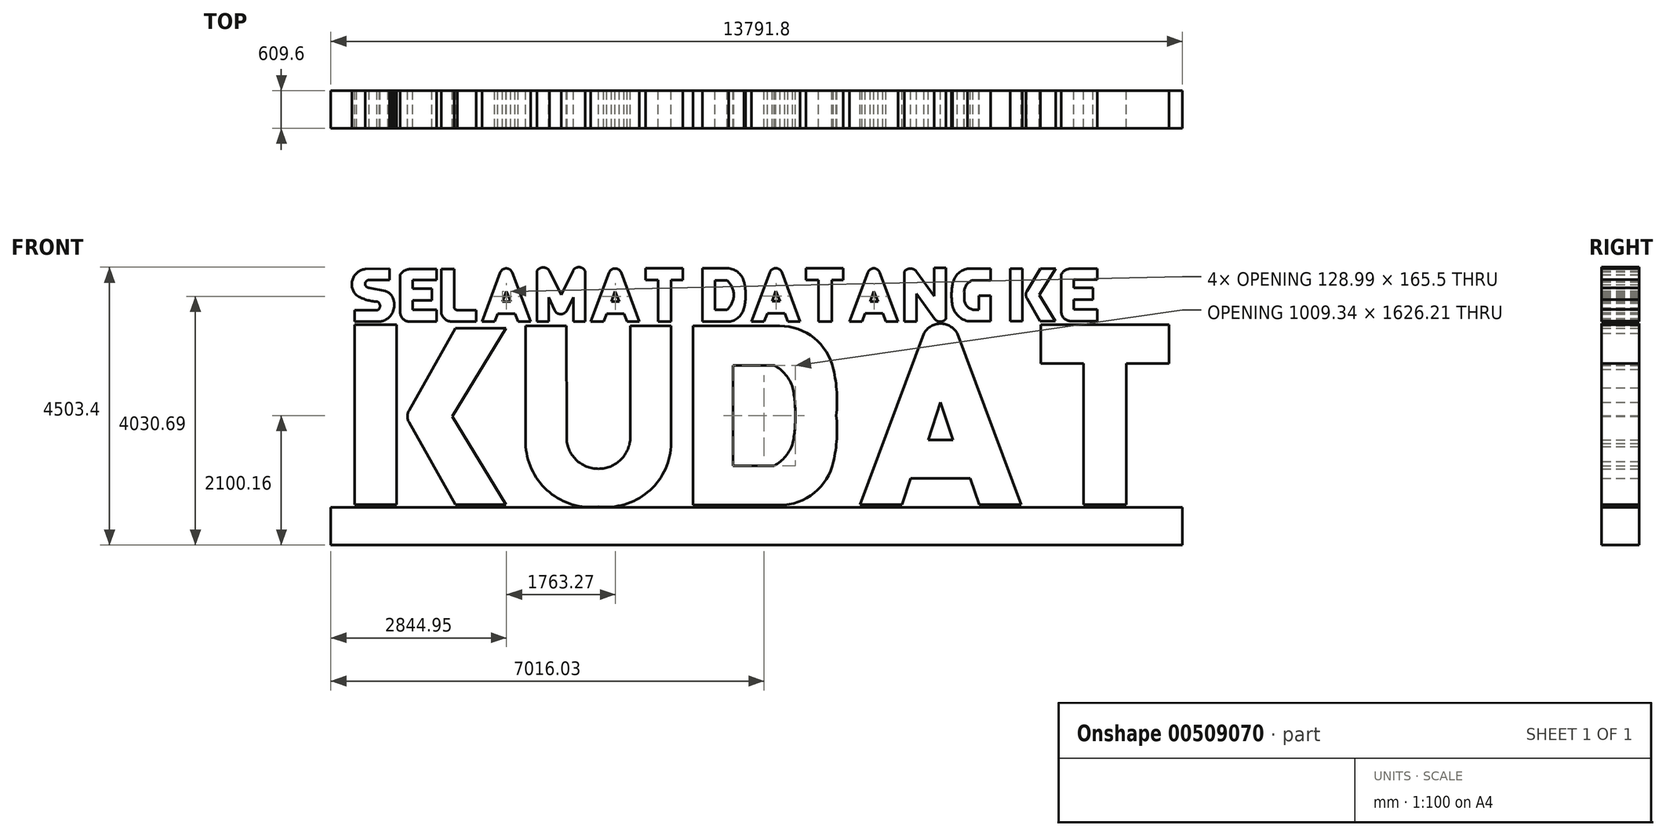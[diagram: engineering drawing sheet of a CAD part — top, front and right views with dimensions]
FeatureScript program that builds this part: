
annotation { "Feature Type Name" : "Feature", "Feature Type Description" : "" }
export const myFeature = defineFeature(function(context is Context, id is Id, definition is map)
    precondition{}
    {
        {
            var Q0;
            Q0=qCreatedBy(makeId("Front.planeOp"),FACE);
            var sketch = newSketch(context, id + "F0", { "sketchPlane" : qUnion([Q0])});
            skLineSegment(sketch, "E0", {"start": v(879.75, 1714.23) * mm, "end": v(879.75, -240.62) * mm});
            skLineSegment(sketch, "E1", {"start": v(-1444.26, -240.62) * mm, "end": v(879.75, -240.62) * mm, "construction": true});
            skLineSegment(sketch, "E2", {"start": v(1236.83, -1188.64) * mm, "end": v(1236.83, 1714.23) * mm});
            skLineSegment(sketch, "E3", {"start": v(1236.83, 1714.23) * mm, "end": v(2637.34, 1714.23) * mm});
            skArc(sketch, "E4", {"start": v(3508.06, 1010.34) * mm, "mid": v(3197.16, 1516.25) * mm, "end": v(2637.34, 1714.23) * mm});
            skLineSegment(sketch, "E5", {"start": v(1236.83, 262.8) * mm, "end": v(3663.8, 262.8) * mm, "construction": true});
            skPoint(sketch, "E5.endSnap0", {"position": v(1236.83, 262.8) * mm});
            skArc(sketch, "E6", {"start": v(3554.76, 262.8) * mm, "mid": v(3561.92, 638.47) * mm, "end": v(3508.06, 1010.34) * mm});
            skArc(sketch, "E7.MirrorCS", {"start": v(3554.76, 262.8) * mm, "mid": v(3561.92, -112.89) * mm, "end": v(3508.06, -484.75) * mm});
            skArc(sketch, "E8.MirrorCS", {"start": v(3508.06, -484.75) * mm, "mid": v(3197.16, -990.66) * mm, "end": v(2637.34, -1188.64) * mm});
            skLineSegment(sketch, "E9.MirrorCS", {"start": v(1236.83, -1188.64) * mm, "end": v(2637.34, -1188.64) * mm});
            skArc(sketch, "E10", {"start": v(2849.13, -189.28) * mm, "mid": v(2883.14, 43.13) * mm, "end": v(2889.18, 277.93) * mm});
            skArc(sketch, "E11", {"start": v(2548.8, -550.31) * mm, "mid": v(2732.4, -397.6) * mm, "end": v(2849.13, -189.28) * mm});
            skLineSegment(sketch, "E12", {"start": v(2548.8, -550.31) * mm, "end": v(1880.98, -550.31) * mm});
            skLineSegment(sketch, "E13", {"start": v(879.75, 1714.23) * mm, "end": v(218.23, 1714.23) * mm});
            skLineSegment(sketch, "E14", {"start": v(218.23, 1714.23) * mm, "end": v(218.23, -87.55) * mm});
            skLineSegment(sketch, "E15", {"start": v(7558.08, 1103.12) * mm, "end": v(7558.08, -1179.44) * mm});
            skLineSegment(sketch, "E16", {"start": v(7558.08, -1179.44) * mm, "end": v(8251.82, -1179.44) * mm});
            skLineSegment(sketch, "E17", {"start": v(7558.08, 1103.12) * mm, "end": v(6867.65, 1103.12) * mm});
            skLineSegment(sketch, "E18", {"start": v(6867.65, 1103.12) * mm, "end": v(6867.65, 1734.9) * mm});
            skLineSegment(sketch, "E19", {"start": v(7904.95, -1179.44) * mm, "end": v(7904.95, 2382.64) * mm, "construction": true});
            skLineSegment(sketch, "E20.MirrorCS", {"start": v(8251.82, 1103.12) * mm, "end": v(8251.82, -1179.44) * mm});
            skLineSegment(sketch, "E21.MirrorCS", {"start": v(8251.82, 1103.12) * mm, "end": v(8942.25, 1103.12) * mm});
            skLineSegment(sketch, "E22.MirrorCS", {"start": v(8942.25, 1103.12) * mm, "end": v(8942.25, 1734.9) * mm});
            skLineSegment(sketch, "E23", {"start": v(6867.65, 1734.9) * mm, "end": v(8942.25, 1734.9) * mm});
            skLineSegment(sketch, "E24", {"start": v(-4247.95, 1734.9) * mm, "end": v(-3569.34, 1734.9) * mm});
            skLineSegment(sketch, "E25", {"start": v(-3569.34, 1734.9) * mm, "end": v(-3569.34, -1181.26) * mm});
            skLineSegment(sketch, "E26", {"start": v(-3569.34, -1181.26) * mm, "end": v(-4247.95, -1181.26) * mm});
            skLineSegment(sketch, "E27", {"start": v(-4247.95, -1181.26) * mm, "end": v(-4247.95, 1734.9) * mm});
            skPoint(sketch, "E28.endSnap0", {"position": v(-3569.34, 276.82) * mm});
            skLineSegment(sketch, "E29", {"start": v(4761.3, -753.34) * mm, "end": v(5725.65, -753.34) * mm});
            skLineSegment(sketch, "E30", {"start": v(5725.65, -753.34) * mm, "end": v(5868.51, -1179.44) * mm});
            skLineSegment(sketch, "E31", {"start": v(5868.51, -1179.44) * mm, "end": v(6547.12, -1179.44) * mm});
            skLineSegment(sketch, "E32", {"start": v(6547.12, -1179.44) * mm, "end": v(5511.35, 1595.4) * mm});
            skLineSegment(sketch, "E33", {"start": v(5243.48, -753.34) * mm, "end": v(5243.48, 1965.8) * mm, "construction": true});
            skLineSegment(sketch, "E34", {"start": v(5243.48, 479.15) * mm, "end": v(5444.33, -133.18) * mm});
            skLineSegment(sketch, "E35", {"start": v(5444.33, -133.18) * mm, "end": v(5243.48, -133.18) * mm});
            skLineSegment(sketch, "E36.MirrorCS", {"start": v(3939.83, -1179.44) * mm, "end": v(4975.6, 1595.4) * mm});
            skLineSegment(sketch, "E37.MirrorCS", {"start": v(4618.44, -1179.44) * mm, "end": v(3939.83, -1179.44) * mm});
            skLineSegment(sketch, "E38.MirrorCS", {"start": v(4761.3, -753.34) * mm, "end": v(4618.44, -1179.44) * mm});
            skLineSegment(sketch, "E39.MirrorCS", {"start": v(5243.48, 479.15) * mm, "end": v(5042.62, -133.18) * mm});
            skLineSegment(sketch, "E40.MirrorCS", {"start": v(5042.62, -133.18) * mm, "end": v(5243.48, -133.18) * mm});
            skArc(sketch, "E41", {"start": v(5511.35, 1595.4) * mm, "mid": v(5243.48, 1750.87) * mm, "end": v(4975.6, 1595.4) * mm});
            skLineSegment(sketch, "E42.MirrorCS", {"start": v(2548.8, 1075.9) * mm, "end": v(1880.98, 1075.9) * mm});
            skArc(sketch, "E43.MirrorCS", {"start": v(2548.8, 1075.9) * mm, "mid": v(2732.4, 923.2) * mm, "end": v(2849.13, 714.87) * mm});
            skArc(sketch, "E44.MirrorCS", {"start": v(2849.13, 714.87) * mm, "mid": v(2883.14, 482.46) * mm, "end": v(2889.18, 247.66) * mm});
            skLineSegment(sketch, "E45", {"start": v(1880.98, 1075.9) * mm, "end": v(1880.98, -550.31) * mm});
            skLineSegment(sketch, "E46", {"start": v(-298.78, 1772.69) * mm, "end": v(-296.6, -1275.31) * mm, "construction": true});
            skArc(sketch, "E47", {"start": v(-297.09, -599.74) * mm, "mid": v(67.1, -450.83) * mm, "end": v(218.23, -87.55) * mm});
            skArc(sketch, "E48", {"start": v(-296.65, -1213.76) * mm, "mid": v(499.5, -978.57) * mm, "end": v(879.75, -240.62) * mm});
            skLineSegment(sketch, "E49.MirrorCS", {"start": v(-815.7, 1713.49) * mm, "end": v(-813.14, -88.29) * mm});
            skLineSegment(sketch, "E50.MirrorCS", {"start": v(-1477.22, 1712.55) * mm, "end": v(-815.7, 1713.49) * mm});
            skLineSegment(sketch, "E51.MirrorCS", {"start": v(-1477.22, 1712.55) * mm, "end": v(-1474.44, -242.3) * mm});
            skArc(sketch, "E52.MirrorCS", {"start": v(-297.09, -599.74) * mm, "mid": v(-661.5, -451.35) * mm, "end": v(-813.14, -88.29) * mm});
            skArc(sketch, "E53.MirrorCS", {"start": v(-296.65, -1213.76) * mm, "mid": v(-1093.13, -979.7) * mm, "end": v(-1474.44, -242.3) * mm});
            skPoint(sketch, "E54.endSnap0", {"position": v(-4297.8, 248.69) * mm});
            skLineSegment(sketch, "E55", {"start": v(-4297.8, 248.69) * mm, "end": v(-2170.88, 248.69) * mm, "construction": true});
            skLineSegment(sketch, "E56", {"start": v(-2615.55, -1181.26) * mm, "end": v(-1793.19, -1181.26) * mm});
            skLineSegment(sketch, "E57", {"start": v(-1793.19, -1181.26) * mm, "end": v(-2665.18, 248.69) * mm});
            skLineSegment(sketch, "E58", {"start": v(-2615.55, -1181.26) * mm, "end": v(-3366.35, 151.64) * mm});
            skLineSegment(sketch, "E59.MirrorCS", {"start": v(-1793.19, 1678.63) * mm, "end": v(-2665.18, 248.69) * mm});
            skLineSegment(sketch, "E60.MirrorCS", {"start": v(-2615.55, 1678.63) * mm, "end": v(-3366.35, 345.74) * mm});
            skLineSegment(sketch, "E61.MirrorCS", {"start": v(-2615.55, 1678.63) * mm, "end": v(-1793.19, 1678.63) * mm});
            skArc(sketch, "E62", {"start": v(-3366.35, 345.74) * mm, "mid": v(-3391.8, 248.69) * mm, "end": v(-3366.35, 151.64) * mm});
            skSolve(sketch);
        }
        {
            var Q0;
            Q0=makeQuery(id+"F0.imprint","IMPRINT",FACE,{"disambiguationData":[TD([[makeQuery(id+"F0.imprint","IMPRINT",EDGE,{"derivedFrom":sQuery(id+"F0.wireOp",EDGE,"E24")}),-1.0]])]});
            var Q1;
            Q1=makeQuery(id+"F0.imprint","IMPRINT",FACE,{"disambiguationData":[TD([[makeQuery(id+"F0.imprint","IMPRINT",EDGE,{"derivedFrom":sQuery(id+"F0.wireOp",EDGE,"E56")}),1.0]])]});
            var Q2;
            Q2=makeQuery(id+"F0.imprint","IMPRINT",FACE,{"disambiguationData":[TD([[makeQuery(id+"F0.imprint","IMPRINT",EDGE,{"derivedFrom":sQuery(id+"F0.wireOp",EDGE,"E0")}),-1.0]])]});
            var Q3;
            Q3=makeQuery(id+"F0.imprint","IMPRINT",FACE,{"disambiguationData":[TD([[makeQuery(id+"F0.imprint","IMPRINT",EDGE,{"derivedFrom":sQuery(id+"F0.wireOp",EDGE,"E2")}),-1.0]])]});
            var Q4;
            Q4=makeQuery(id+"F0.imprint","IMPRINT",FACE,{"disambiguationData":[TD([[makeQuery(id+"F0.imprint","IMPRINT",EDGE,{"derivedFrom":sQuery(id+"F0.wireOp",EDGE,"E29")}),1.0]])]});
            var Q5;
            Q5=makeQuery(id+"F0.imprint","IMPRINT",FACE,{"disambiguationData":[TD([[makeQuery(id+"F0.imprint","IMPRINT",EDGE,{"derivedFrom":sQuery(id+"F0.wireOp",EDGE,"E15")}),1.0]])]});
            extrude(context, id + "F1", {"entities" : qUnion([Q0, Q1, Q2, Q3, Q4, Q5]), "depth" : 609.6 * mm});
        }
        {
            var Q0;
            Q0=qCreatedBy(makeId("Front.planeOp"),FACE);
            var sketch = newSketch(context, id + "F2", { "sketchPlane" : qUnion([Q0])});
            skLineSegment(sketch, "E63", {"start": v(-4630.38, -1227.77) * mm, "end": v(9161.42, -1227.77) * mm});
            skLineSegment(sketch, "E64", {"start": v(-4630.38, -1227.77) * mm, "end": v(-4630.38, -1837.37) * mm});
            skLineSegment(sketch, "E65", {"start": v(-4630.38, -1837.37) * mm, "end": v(9161.42, -1837.37) * mm});
            skLineSegment(sketch, "E66", {"start": v(9161.42, -1227.77) * mm, "end": v(9161.42, -1837.37) * mm});
            skSolve(sketch);
        }
        {
            var Q0;
            Q0 = qSketchRegion(id + "F2", true);
            extrude(context, id + "F3", {"entities" : qUnion([Q0]), "depth" : 609.6 * mm});
        }
        {
            var Q0;
            Q0=qCreatedBy(makeId("Front.planeOp"),FACE);
            var sketch = newSketch(context, id + "F4", { "sketchPlane" : qUnion([Q0])});
            skLineSegment(sketch, "E67", {"start": v(-3679.21, 2642.46) * mm, "end": v(-3683.77, 2457.03) * mm});
            skLineSegment(sketch, "E68", {"start": v(-3683.77, 2457.03) * mm, "end": v(-4013.6, 2457.03) * mm});
            skArc(sketch, "E69", {"start": v(-4013.6, 2457.03) * mm, "mid": v(-4075.95, 2392.35) * mm, "end": v(-4009.03, 2332.4) * mm});
            skLineSegment(sketch, "E70", {"start": v(-4009.03, 2332.4) * mm, "end": v(-3750.23, 2278.24) * mm});
            skArc(sketch, "E71", {"start": v(-3636.31, 2183.66) * mm, "mid": v(-3681.54, 2245.09) * mm, "end": v(-3750.23, 2278.24) * mm});
            skArc(sketch, "E72", {"start": v(-3705.1, 1837.6) * mm, "mid": v(-3609.6, 1998.49) * mm, "end": v(-3636.31, 2183.66) * mm});
            skArc(sketch, "E73", {"start": v(-3846.96, 1783.86) * mm, "mid": v(-3771.86, 1799.73) * mm, "end": v(-3705.1, 1837.6) * mm});
            skLineSegment(sketch, "E74", {"start": v(-3846.96, 1783.86) * mm, "end": v(-4246.76, 1783.86) * mm});
            skLineSegment(sketch, "E75", {"start": v(-4246.76, 1783.86) * mm, "end": v(-4246.76, 1966.57) * mm});
            skLineSegment(sketch, "E76", {"start": v(-4246.76, 1966.57) * mm, "end": v(-3881.35, 1966.57) * mm});
            skArc(sketch, "E77", {"start": v(-3881.35, 1966.57) * mm, "mid": v(-3834.4, 2037.5) * mm, "end": v(-3881.35, 2108.43) * mm});
            skArc(sketch, "E78", {"start": v(-4212.83, 2209.12) * mm, "mid": v(-4054.08, 2135.77) * mm, "end": v(-3881.35, 2108.43) * mm});
            skArc(sketch, "E79", {"start": v(-4075.95, 2633.11) * mm, "mid": v(-4280.39, 2465.02) * mm, "end": v(-4212.83, 2209.12) * mm});
            skPoint(sketch, "E79.startSnap0", {"position": v(-4075.95, 2392.35) * mm});
            skLineSegment(sketch, "E80", {"start": v(-4075.95, 2633.11) * mm, "end": v(-3679.21, 2642.46) * mm});
            skLineSegment(sketch, "E81", {"start": v(-2921.7, 2633.11) * mm, "end": v(-2921.7, 2457.03) * mm});
            skLineSegment(sketch, "E82", {"start": v(-2921.7, 2457.03) * mm, "end": v(-3303.56, 2457.03) * mm});
            skLineSegment(sketch, "E83", {"start": v(-3303.56, 2457.03) * mm, "end": v(-3303.56, 2321.01) * mm});
            skLineSegment(sketch, "E84", {"start": v(-3303.56, 2321.01) * mm, "end": v(-2991.89, 2321.01) * mm});
            skLineSegment(sketch, "E85", {"start": v(-2991.89, 2321.01) * mm, "end": v(-2991.89, 2129.71) * mm});
            skLineSegment(sketch, "E86", {"start": v(-2991.89, 2129.71) * mm, "end": v(-3303.56, 2129.71) * mm});
            skLineSegment(sketch, "E87", {"start": v(-3303.56, 2129.71) * mm, "end": v(-3303.56, 1972.8) * mm});
            skLineSegment(sketch, "E88", {"start": v(-3303.56, 1972.8) * mm, "end": v(-2921.7, 1972.8) * mm});
            skLineSegment(sketch, "E89", {"start": v(-2921.7, 1972.8) * mm, "end": v(-2921.7, 1783.86) * mm});
            skLineSegment(sketch, "E90", {"start": v(-2921.7, 1783.86) * mm, "end": v(-3353.28, 1783.86) * mm});
            skLineSegment(sketch, "E91", {"start": v(-2921.7, 2633.11) * mm, "end": v(-3351.06, 2633.11) * mm});
            skArc(sketch, "E92", {"start": v(-3351.06, 2633.11) * mm, "mid": v(-3441.89, 2608.11) * mm, "end": v(-3507.12, 2540.16) * mm});
            skArc(sketch, "E93", {"start": v(-3507.12, 1919.95) * mm, "mid": v(-3455.98, 1822.77) * mm, "end": v(-3353.28, 1783.86) * mm});
            skLineSegment(sketch, "E94", {"start": v(-3507.12, 2540.16) * mm, "end": v(-3507.12, 1919.95) * mm});
            skLineSegment(sketch, "E95", {"start": v(-2839.54, 2633.11) * mm, "end": v(-2632.84, 2633.11) * mm});
            skLineSegment(sketch, "E96", {"start": v(-2632.84, 2633.11) * mm, "end": v(-2632.84, 2019.12) * mm});
            skArc(sketch, "E97", {"start": v(-2632.84, 2019.12) * mm, "mid": v(-2618.2, 1984.36) * mm, "end": v(-2583.13, 1970.52) * mm});
            skLineSegment(sketch, "E98", {"start": v(-2583.13, 1970.52) * mm, "end": v(-2277.9, 1970.52) * mm});
            skLineSegment(sketch, "E99", {"start": v(-2277.9, 1970.52) * mm, "end": v(-2277.9, 1783.86) * mm});
            skLineSegment(sketch, "E100", {"start": v(-2277.9, 1783.86) * mm, "end": v(-2668.29, 1783.86) * mm});
            skArc(sketch, "E101", {"start": v(-2839.54, 1914.99) * mm, "mid": v(-2776.13, 1820.4) * mm, "end": v(-2668.29, 1783.86) * mm});
            skLineSegment(sketch, "E102", {"start": v(-2839.54, 2633.11) * mm, "end": v(-2839.54, 1914.99) * mm});
            skLineSegment(sketch, "E103", {"start": v(-2184.46, 1783.86) * mm, "end": v(-1979.96, 1783.86) * mm});
            skPoint(sketch, "E103.startSnap0", {"position": v(-2473.1, 1783.86) * mm});
            skLineSegment(sketch, "E104", {"start": v(-1979.96, 1783.86) * mm, "end": v(-1928.84, 1914.99) * mm});
            skLineSegment(sketch, "E105", {"start": v(-1928.84, 1914.99) * mm, "end": v(-1647.66, 1914.99) * mm});
            skLineSegment(sketch, "E106", {"start": v(-1647.66, 1914.99) * mm, "end": v(-1596.54, 1783.86) * mm});
            skLineSegment(sketch, "E107", {"start": v(-1596.54, 1783.86) * mm, "end": v(-1397.16, 1783.86) * mm});
            skLineSegment(sketch, "E108", {"start": v(-1397.16, 1783.86) * mm, "end": v(-1693.67, 2578.85) * mm});
            skArc(sketch, "E109", {"start": v(-1693.67, 2578.85) * mm, "mid": v(-1790.8, 2646.29) * mm, "end": v(-1887.94, 2578.85) * mm});
            skLineSegment(sketch, "E110", {"start": v(-2184.46, 1783.86) * mm, "end": v(-1887.94, 2578.85) * mm});
            skLineSegment(sketch, "E111", {"start": v(-1790.8, 2276.07) * mm, "end": v(-1720.94, 2110.57) * mm});
            skLineSegment(sketch, "E112", {"start": v(-1720.94, 2110.57) * mm, "end": v(-1849.93, 2110.57) * mm});
            skLineSegment(sketch, "E113", {"start": v(-1849.93, 2110.57) * mm, "end": v(-1790.8, 2276.07) * mm});
            skLineSegment(sketch, "E114", {"start": v(-1293.3, 1783.86) * mm, "end": v(-1099.85, 1783.86) * mm});
            skLineSegment(sketch, "E115", {"start": v(-1099.85, 1783.86) * mm, "end": v(-1099.85, 2178.77) * mm});
            skLineSegment(sketch, "E116", {"start": v(-1293.3, 1783.86) * mm, "end": v(-1293.3, 2604.82) * mm});
            skArc(sketch, "E117", {"start": v(-1091.07, 2604.82) * mm, "mid": v(-1192.18, 2660.73) * mm, "end": v(-1293.3, 2604.82) * mm});
            skLineSegment(sketch, "E118", {"start": v(-1091.07, 2604.82) * mm, "end": v(-902.32, 2218.39) * mm});
            skLineSegment(sketch, "E119", {"start": v(-902.32, 2218.39) * mm, "end": v(-711.79, 2604.82) * mm});
            skArc(sketch, "E120", {"start": v(-514.96, 2604.82) * mm, "mid": v(-613.37, 2666.03) * mm, "end": v(-711.79, 2604.82) * mm});
            skLineSegment(sketch, "E121", {"start": v(-514.96, 2604.82) * mm, "end": v(-514.96, 1782.01) * mm});
            skLineSegment(sketch, "E122", {"start": v(-514.96, 1782.01) * mm, "end": v(-703.32, 1782.01) * mm});
            skLineSegment(sketch, "E123", {"start": v(-703.32, 1782.01) * mm, "end": v(-703.32, 2178.77) * mm});
            skLineSegment(sketch, "E124", {"start": v(-703.32, 2178.77) * mm, "end": v(-804.31, 1970.52) * mm});
            skLineSegment(sketch, "E125", {"start": v(-1099.85, 2178.77) * mm, "end": v(-1007.98, 1970.52) * mm});
            skArc(sketch, "E126", {"start": v(-1007.98, 1970.52) * mm, "mid": v(-906.15, 1904.14) * mm, "end": v(-804.31, 1970.52) * mm});
            skLineSegment(sketch, "E127", {"start": v(667.07, 2457.3) * mm, "end": v(667.07, 1782.01) * mm});
            skLineSegment(sketch, "E128", {"start": v(667.07, 1782.01) * mm, "end": v(881.79, 1782.01) * mm});
            skLineSegment(sketch, "E129", {"start": v(881.79, 1782.01) * mm, "end": v(881.79, 2457.3) * mm});
            skLineSegment(sketch, "E130", {"start": v(881.79, 2457.3) * mm, "end": v(1070.94, 2457.3) * mm});
            skLineSegment(sketch, "E131", {"start": v(1070.94, 2457.3) * mm, "end": v(1070.94, 2645.52) * mm});
            skLineSegment(sketch, "E132", {"start": v(1070.94, 2645.52) * mm, "end": v(464.02, 2645.52) * mm});
            skLineSegment(sketch, "E133", {"start": v(464.02, 2645.52) * mm, "end": v(464.02, 2457.3) * mm});
            skLineSegment(sketch, "E134", {"start": v(667.07, 2457.3) * mm, "end": v(464.02, 2457.3) * mm});
            skLineSegment(sketch, "E135", {"start": v(-421.19, 1781.94) * mm, "end": v(-216.7, 1781.94) * mm});
            skLineSegment(sketch, "E136", {"start": v(-216.7, 1781.94) * mm, "end": v(-165.57, 1913.06) * mm});
            skLineSegment(sketch, "E137", {"start": v(-165.57, 1913.06) * mm, "end": v(115.6, 1913.06) * mm});
            skLineSegment(sketch, "E138", {"start": v(115.6, 1913.06) * mm, "end": v(166.73, 1781.94) * mm});
            skLineSegment(sketch, "E139", {"start": v(166.73, 1781.94) * mm, "end": v(366.1, 1781.94) * mm});
            skLineSegment(sketch, "E140", {"start": v(366.1, 1781.94) * mm, "end": v(69.6, 2576.92) * mm});
            skArc(sketch, "E141", {"start": v(69.6, 2576.92) * mm, "mid": v(-27.54, 2644.36) * mm, "end": v(-124.68, 2576.92) * mm});
            skLineSegment(sketch, "E142", {"start": v(-421.19, 1781.94) * mm, "end": v(-124.68, 2576.92) * mm});
            skLineSegment(sketch, "E143", {"start": v(-27.54, 2274.15) * mm, "end": v(42.33, 2108.65) * mm});
            skLineSegment(sketch, "E144", {"start": v(42.33, 2108.65) * mm, "end": v(-86.66, 2108.65) * mm});
            skLineSegment(sketch, "E145", {"start": v(-86.66, 2108.65) * mm, "end": v(-27.54, 2274.15) * mm});
            skLineSegment(sketch, "E146", {"start": v(-514.96, 1782.01) * mm, "end": v(481.15, 1782.01) * mm, "construction": true});
            skLineSegment(sketch, "E147", {"start": v(1387.1, 2646.04) * mm, "end": v(1387.1, 1782.01) * mm});
            skLineSegment(sketch, "E148", {"start": v(1387.1, 1782.01) * mm, "end": v(1814, 1782.01) * mm});
            skArc(sketch, "E149", {"start": v(1814, 1782.01) * mm, "mid": v(1973.74, 1853.6) * mm, "end": v(2061.74, 2004.93) * mm});
            skLineSegment(sketch, "E150", {"start": v(1387.1, 2214.03) * mm, "end": v(2207.83, 2214.03) * mm, "construction": true});
            skPoint(sketch, "E150.endSnap0", {"position": v(1387.1, 2214.03) * mm});
            skLineSegment(sketch, "E151", {"start": v(1590.37, 2214.03) * mm, "end": v(1590.37, 1975.72) * mm});
            skLineSegment(sketch, "E152", {"start": v(1590.37, 1975.72) * mm, "end": v(1786.44, 1975.72) * mm});
            skArc(sketch, "E153", {"start": v(1786.44, 1975.72) * mm, "mid": v(1864.52, 2083.95) * mm, "end": v(1894.35, 2214.03) * mm});
            skArc(sketch, "E154", {"start": v(2061.74, 2004.93) * mm, "mid": v(2079.63, 2108.78) * mm, "end": v(2084.96, 2214.03) * mm});
            skArc(sketch, "E155.MirrorCS", {"start": v(1786.44, 2452.34) * mm, "mid": v(1864.52, 2344.1) * mm, "end": v(1894.35, 2214.03) * mm});
            skLineSegment(sketch, "E156.MirrorCS", {"start": v(1590.37, 2452.34) * mm, "end": v(1786.44, 2452.34) * mm});
            skLineSegment(sketch, "E157.MirrorCS", {"start": v(1590.37, 2214.03) * mm, "end": v(1590.37, 2452.34) * mm});
            skArc(sketch, "E158.MirrorCS", {"start": v(2061.74, 2423.13) * mm, "mid": v(2079.63, 2319.28) * mm, "end": v(2084.96, 2214.03) * mm});
            skArc(sketch, "E159.MirrorCS", {"start": v(1814, 2646.04) * mm, "mid": v(1973.74, 2574.45) * mm, "end": v(2061.74, 2423.13) * mm});
            skLineSegment(sketch, "E160", {"start": v(1387.1, 2646.04) * mm, "end": v(1814, 2646.04) * mm});
            skLineSegment(sketch, "E161", {"start": v(7783.5, 2641.2) * mm, "end": v(7783.5, 2465.1) * mm});
            skLineSegment(sketch, "E162", {"start": v(7783.5, 2465.1) * mm, "end": v(7401.64, 2465.1) * mm});
            skLineSegment(sketch, "E163", {"start": v(7401.64, 2465.1) * mm, "end": v(7401.64, 2329.1) * mm});
            skLineSegment(sketch, "E164", {"start": v(7401.64, 2329.1) * mm, "end": v(7713.32, 2329.1) * mm});
            skLineSegment(sketch, "E165", {"start": v(7713.32, 2329.1) * mm, "end": v(7713.32, 2137.79) * mm});
            skLineSegment(sketch, "E166", {"start": v(7713.32, 2137.79) * mm, "end": v(7401.64, 2137.79) * mm});
            skLineSegment(sketch, "E167", {"start": v(7401.64, 2137.79) * mm, "end": v(7401.64, 1980.88) * mm});
            skLineSegment(sketch, "E168", {"start": v(7401.64, 1980.88) * mm, "end": v(7783.5, 1980.88) * mm});
            skLineSegment(sketch, "E169", {"start": v(7783.5, 1980.88) * mm, "end": v(7783.5, 1791.94) * mm});
            skLineSegment(sketch, "E170", {"start": v(7783.5, 1791.94) * mm, "end": v(7351.92, 1791.94) * mm});
            skLineSegment(sketch, "E171", {"start": v(7783.5, 2641.2) * mm, "end": v(7354.14, 2641.2) * mm});
            skArc(sketch, "E172", {"start": v(7354.14, 2641.2) * mm, "mid": v(7263.32, 2616.2) * mm, "end": v(7198.08, 2548.23) * mm});
            skArc(sketch, "E173", {"start": v(7198.08, 1928.03) * mm, "mid": v(7249.22, 1830.84) * mm, "end": v(7351.92, 1791.94) * mm});
            skLineSegment(sketch, "E174", {"start": v(7198.08, 2548.23) * mm, "end": v(7198.08, 1928.03) * mm});
            skLineSegment(sketch, "E175", {"start": v(2181.95, 1786.3) * mm, "end": v(2386.44, 1786.3) * mm});
            skLineSegment(sketch, "E176", {"start": v(2386.44, 1786.3) * mm, "end": v(2437.56, 1917.42) * mm});
            skLineSegment(sketch, "E177", {"start": v(2437.56, 1917.42) * mm, "end": v(2718.74, 1917.42) * mm});
            skLineSegment(sketch, "E178", {"start": v(2718.74, 1917.42) * mm, "end": v(2769.86, 1786.3) * mm});
            skLineSegment(sketch, "E179", {"start": v(2769.86, 1786.3) * mm, "end": v(2969.24, 1786.3) * mm});
            skLineSegment(sketch, "E180", {"start": v(2969.24, 1786.3) * mm, "end": v(2672.73, 2581.28) * mm});
            skArc(sketch, "E181", {"start": v(2672.73, 2581.28) * mm, "mid": v(2575.6, 2648.72) * mm, "end": v(2478.46, 2581.28) * mm});
            skLineSegment(sketch, "E182", {"start": v(2181.95, 1786.3) * mm, "end": v(2478.46, 2581.28) * mm});
            skLineSegment(sketch, "E183", {"start": v(2575.6, 2278.5) * mm, "end": v(2645.47, 2113) * mm});
            skLineSegment(sketch, "E184", {"start": v(2645.47, 2113) * mm, "end": v(2516.47, 2113) * mm});
            skLineSegment(sketch, "E185", {"start": v(2516.47, 2113) * mm, "end": v(2575.6, 2278.5) * mm});
            skLineSegment(sketch, "E186", {"start": v(1090.07, 1782.01) * mm, "end": v(3080.12, 1782.01) * mm, "construction": true});
            skLineSegment(sketch, "E187", {"start": v(3264.8, 2459.4) * mm, "end": v(3264.8, 1784.1) * mm});
            skLineSegment(sketch, "E188", {"start": v(3264.8, 1784.1) * mm, "end": v(3479.52, 1784.1) * mm});
            skLineSegment(sketch, "E189", {"start": v(3479.52, 1784.1) * mm, "end": v(3479.52, 2459.4) * mm});
            skLineSegment(sketch, "E190", {"start": v(3479.52, 2459.4) * mm, "end": v(3668.68, 2459.4) * mm});
            skLineSegment(sketch, "E191", {"start": v(3668.68, 2459.4) * mm, "end": v(3668.68, 2647.6) * mm});
            skLineSegment(sketch, "E192", {"start": v(3668.68, 2647.6) * mm, "end": v(3061.76, 2647.6) * mm});
            skLineSegment(sketch, "E193", {"start": v(3061.76, 2647.6) * mm, "end": v(3061.76, 2459.4) * mm});
            skLineSegment(sketch, "E194", {"start": v(3264.8, 2459.4) * mm, "end": v(3061.76, 2459.4) * mm});
            skLineSegment(sketch, "E195", {"start": v(3768.55, 1784.28) * mm, "end": v(3973.04, 1784.28) * mm});
            skLineSegment(sketch, "E196", {"start": v(3973.04, 1784.28) * mm, "end": v(4024.17, 1915.4) * mm});
            skLineSegment(sketch, "E197", {"start": v(4024.17, 1915.4) * mm, "end": v(4305.35, 1915.4) * mm});
            skLineSegment(sketch, "E198", {"start": v(4305.35, 1915.4) * mm, "end": v(4356.47, 1784.28) * mm});
            skLineSegment(sketch, "E199", {"start": v(4356.47, 1784.28) * mm, "end": v(4555.85, 1784.28) * mm});
            skLineSegment(sketch, "E200", {"start": v(4555.85, 1784.28) * mm, "end": v(4259.33, 2579.26) * mm});
            skArc(sketch, "E201", {"start": v(4259.33, 2579.26) * mm, "mid": v(4162.2, 2646.7) * mm, "end": v(4065.07, 2579.26) * mm});
            skLineSegment(sketch, "E202", {"start": v(3768.55, 1784.28) * mm, "end": v(4065.07, 2579.26) * mm});
            skLineSegment(sketch, "E203", {"start": v(4162.2, 2276.49) * mm, "end": v(4232.07, 2110.99) * mm});
            skLineSegment(sketch, "E204", {"start": v(4232.07, 2110.99) * mm, "end": v(4103.08, 2110.99) * mm});
            skLineSegment(sketch, "E205", {"start": v(4103.08, 2110.99) * mm, "end": v(4162.2, 2276.49) * mm});
            skLineSegment(sketch, "E206", {"start": v(7098.7, 1791.94) * mm, "end": v(6852.91, 1791.94) * mm});
            skLineSegment(sketch, "E207", {"start": v(6852.91, 1791.94) * mm, "end": v(6641.83, 2162.05) * mm});
            skLineSegment(sketch, "E208", {"start": v(7098.7, 1791.94) * mm, "end": v(6841.23, 2213.74) * mm});
            skLineSegment(sketch, "E209", {"start": v(6841.23, 2213.74) * mm, "end": v(7110.96, 2641.2) * mm});
            skLineSegment(sketch, "E210", {"start": v(7110.96, 2641.2) * mm, "end": v(6858.36, 2641.2) * mm});
            skLineSegment(sketch, "E211", {"start": v(6858.36, 2641.2) * mm, "end": v(6641.83, 2281.3) * mm});
            skArc(sketch, "E212", {"start": v(6641.83, 2281.3) * mm, "mid": v(6625.28, 2221.68) * mm, "end": v(6641.83, 2162.05) * mm});
            skLineSegment(sketch, "E213", {"start": v(4656.71, 1784.28) * mm, "end": v(4851.9, 1784.28) * mm});
            skLineSegment(sketch, "E214", {"start": v(4851.9, 1784.28) * mm, "end": v(4851.9, 2232.74) * mm});
            skLineSegment(sketch, "E215", {"start": v(4851.9, 2232.74) * mm, "end": v(5145.14, 1830.31) * mm});
            skArc(sketch, "E216", {"start": v(5145.14, 1830.31) * mm, "mid": v(5238.43, 1782.86) * mm, "end": v(5331.72, 1830.31) * mm});
            skLineSegment(sketch, "E217", {"start": v(5331.72, 1830.31) * mm, "end": v(5331.72, 2652.78) * mm});
            skLineSegment(sketch, "E218", {"start": v(5331.72, 2652.78) * mm, "end": v(5138.2, 2652.78) * mm});
            skLineSegment(sketch, "E219", {"start": v(5138.2, 2652.78) * mm, "end": v(5138.2, 2199.77) * mm});
            skLineSegment(sketch, "E220", {"start": v(5138.2, 2199.77) * mm, "end": v(4854.09, 2593.39) * mm});
            skArc(sketch, "E221", {"start": v(4854.09, 2593.39) * mm, "mid": v(4755.4, 2643.86) * mm, "end": v(4656.71, 2593.39) * mm});
            skLineSegment(sketch, "E222", {"start": v(4656.71, 2593.39) * mm, "end": v(4656.71, 1784.28) * mm});
            skLineSegment(sketch, "E223", {"start": v(6569.3, 2641.2) * mm, "end": v(6373.59, 2641.2) * mm});
            skLineSegment(sketch, "E224", {"start": v(6373.59, 2641.2) * mm, "end": v(6373.59, 1791.94) * mm});
            skLineSegment(sketch, "E225", {"start": v(6373.59, 1791.94) * mm, "end": v(6569.3, 1791.94) * mm});
            skLineSegment(sketch, "E226", {"start": v(6569.3, 1791.94) * mm, "end": v(6569.3, 2641.2) * mm});
            skLineSegment(sketch, "E227", {"start": v(6055.68, 2641.2) * mm, "end": v(6055.68, 2454.83) * mm});
            skLineSegment(sketch, "E228", {"start": v(6055.68, 2454.83) * mm, "end": v(5768.84, 2454.83) * mm});
            skArc(sketch, "E229", {"start": v(5768.84, 2454.83) * mm, "mid": v(5661.36, 2378.63) * mm, "end": v(5625.43, 2251.88) * mm});
            skArc(sketch, "E230", {"start": v(5625.43, 2143.6) * mm, "mid": v(5668.84, 2036.45) * mm, "end": v(5768.84, 1978.45) * mm});
            skLineSegment(sketch, "E231", {"start": v(5625.43, 2251.88) * mm, "end": v(5625.43, 2143.6) * mm});
            skLineSegment(sketch, "E232", {"start": v(5768.84, 1978.45) * mm, "end": v(5866.34, 1978.45) * mm});
            skLineSegment(sketch, "E233", {"start": v(5866.34, 1978.45) * mm, "end": v(5866.34, 2205.82) * mm});
            skLineSegment(sketch, "E234", {"start": v(5866.34, 2205.82) * mm, "end": v(6055.68, 2205.82) * mm});
            skLineSegment(sketch, "E235", {"start": v(6055.68, 2205.82) * mm, "end": v(6055.68, 1791.94) * mm});
            skLineSegment(sketch, "E236", {"start": v(6055.68, 1791.94) * mm, "end": v(5681.67, 1791.94) * mm});
            skArc(sketch, "E237", {"start": v(5429.78, 2084.06) * mm, "mid": v(5508.42, 1897.21) * mm, "end": v(5681.67, 1791.94) * mm});
            skLineSegment(sketch, "E238", {"start": v(6055.68, 2641.2) * mm, "end": v(5681.67, 2641.2) * mm});
            skArc(sketch, "E239", {"start": v(5681.67, 2641.2) * mm, "mid": v(5516.64, 2550.21) * mm, "end": v(5437.02, 2379.4) * mm});
            skArc(sketch, "E240", {"start": v(5437.02, 2379.4) * mm, "mid": v(5420.78, 2232.04) * mm, "end": v(5429.78, 2084.06) * mm});
            skSolve(sketch);
        }
        {
            var Q0;
            Q0 = qSketchRegion(id + "F4", true);
            extrude(context, id + "F5", {"entities" : qUnion([Q0]), "depth" : 609.6 * mm});
        }
    });
